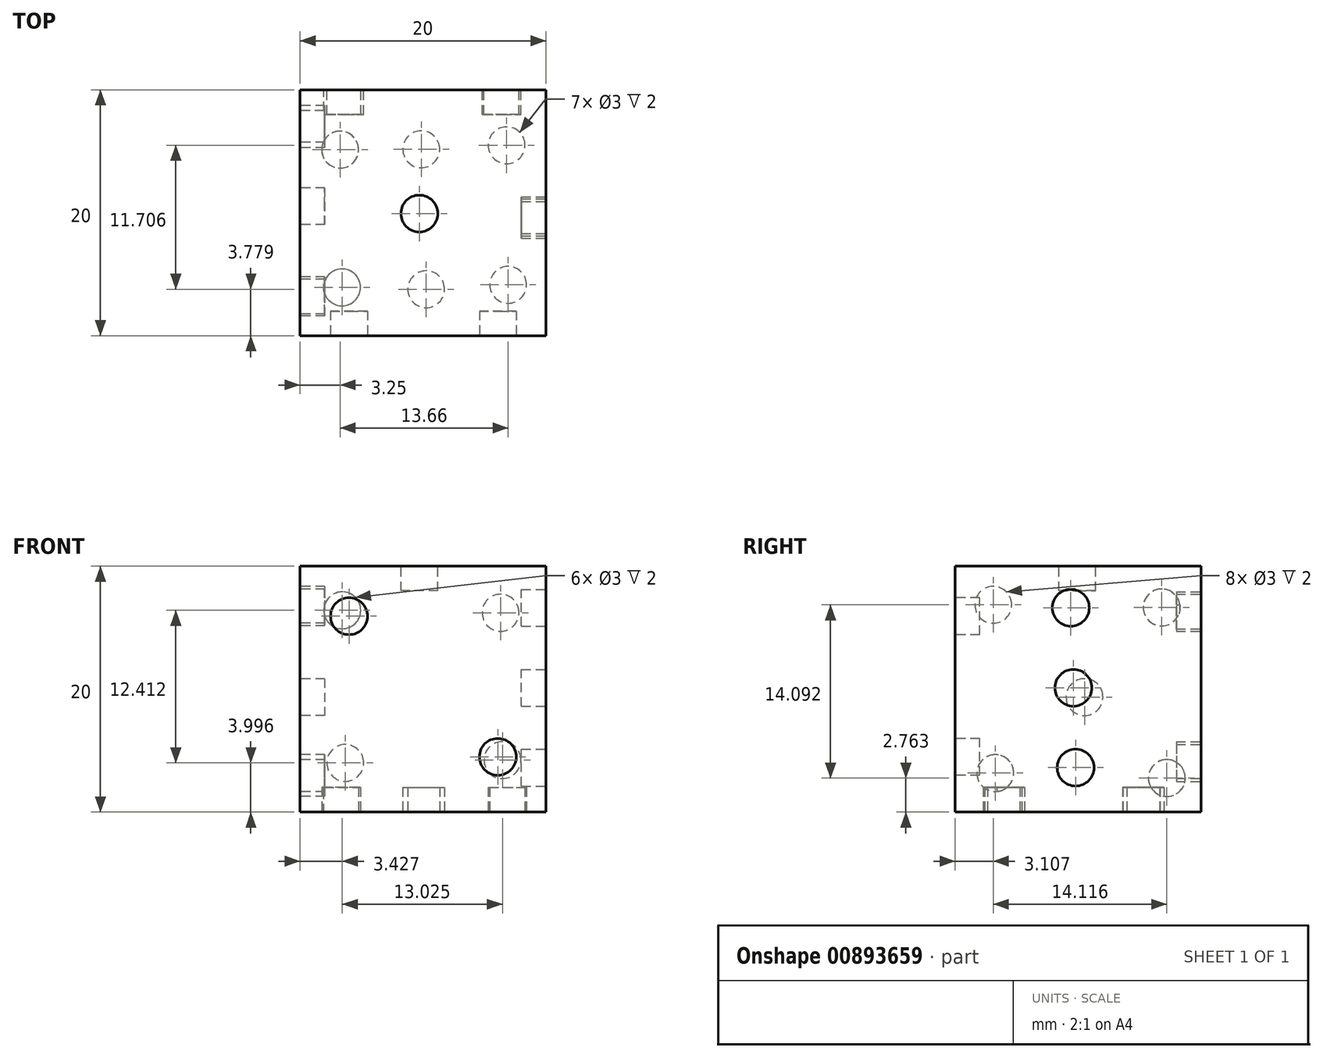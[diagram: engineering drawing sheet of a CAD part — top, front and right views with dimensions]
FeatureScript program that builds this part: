
annotation { "Feature Type Name" : "Feature", "Feature Type Description" : "" }
export const myFeature = defineFeature(function(context is Context, id is Id, definition is map)
    precondition{}
    {
        {
            var Q0;
            Q0=qCreatedBy(makeId("Top.planeOp"),FACE);
            var sketch = newSketch(context, id + "F0", { "sketchPlane" : qUnion([Q0])});
            skLineSegment(sketch, "E0.bottom", {"start": v(-32.53, -1.25) * mm, "end": v(-12.53, -1.25) * mm});
            skLineSegment(sketch, "E0.top", {"start": v(-32.53, -21.25) * mm, "end": v(-12.53, -21.25) * mm});
            skLineSegment(sketch, "E0.left", {"start": v(-32.53, -1.25) * mm, "end": v(-32.53, -21.25) * mm});
            skLineSegment(sketch, "E0.right", {"start": v(-12.53, -1.25) * mm, "end": v(-12.53, -21.25) * mm});
            skSolve(sketch);
        }
        {
            var Q0;
            Q0=makeQuery(id+"F0.imprint","IMPRINT",FACE,{"disambiguationData":[TD([[makeQuery(id+"F0.imprint","IMPRINT",EDGE,{"derivedFrom":sQuery(id+"F0.wireOp",EDGE,"E0.bottom")}),-1.0]])]});
            extrude(context, id + "F1", {"entities" : qUnion([Q0]), "depth" : 20 * mm, "offsetDistance" : 25 * mm});
        }
        {
            var Q0;
            Q0=makeQuery(id+"F1.opExtrude","CAP_FACE",FACE,{"disambiguationData":[OSD([sQuery(id+"F0.wireOp",EDGE,"E0.bottom"),sQuery(id+"F0.wireOp",EDGE,"E0.top"),sQuery(id+"F0.wireOp",EDGE,"E0.left"),sQuery(id+"F0.wireOp",EDGE,"E0.right")])],"isStart":false});
            var sketch = newSketch(context, id + "F2", { "sketchPlane" : qUnion([Q0])});
            skCircle(sketch, "E1", {"center": v(-22.83, -11.32) * mm, "radius": 1.5 * mm});
            skSolve(sketch);
        }
        {
            var Q0;
            Q0 = qSketchRegion(id + "F2", true);
            extrude(context, id + "F3", {"entities" : qUnion([Q0]), "operationType" : NewBodyOperationType.REMOVE, "oppositeDirection" : true, "depth" : 2 * mm, "offsetDistance" : 25 * mm});
        }
        {
            var Q0;
            Q0=makeQuery(id+"F1.opExtrude","SWEPT_FACE",FACE,{"disambiguationData":[OSD([sQuery(id+"F0.wireOp",EDGE,"E0.top")])]});
            var sketch = newSketch(context, id + "F4", { "sketchPlane" : qUnion([Q0])});
            skCircle(sketch, "E2", {"center": v(-28.56, 15.93) * mm, "radius": 1.5 * mm});
            skCircle(sketch, "E3", {"center": v(-16.45, 4.48) * mm, "radius": 1.5 * mm});
            skSolve(sketch);
        }
        {
            var Q0;
            Q0 = qSketchRegion(id + "F4", true);
            extrude(context, id + "F5", {"entities" : qUnion([Q0]), "operationType" : NewBodyOperationType.REMOVE, "oppositeDirection" : true, "depth" : 2 * mm, "offsetDistance" : 25 * mm});
        }
        {
            var Q0;
            Q0=makeQuery(id+"F1.opExtrude","SWEPT_FACE",FACE,{"disambiguationData":[OSD([sQuery(id+"F0.wireOp",EDGE,"E0.right")])]});
            var sketch = newSketch(context, id + "F6", { "sketchPlane" : qUnion([Q0])});
            skCircle(sketch, "E4", {"center": v(-11.84, 16.62) * mm, "radius": 1.5 * mm});
            skCircle(sketch, "E5", {"center": v(-11.45, 3.61) * mm, "radius": 1.5 * mm});
            skCircle(sketch, "E6", {"center": v(-11.63, 10.1) * mm, "radius": 1.5 * mm});
            skSolve(sketch);
        }
        {
            var Q0;
            Q0 = qSketchRegion(id + "F6", true);
            extrude(context, id + "F7", {"entities" : qUnion([Q0]), "operationType" : NewBodyOperationType.REMOVE, "oppositeDirection" : true, "depth" : 2 * mm, "offsetDistance" : 25 * mm});
        }
        {
            var Q0;
            Q0=makeQuery(id+"F1.opExtrude","SWEPT_FACE",FACE,{"disambiguationData":[OSD([sQuery(id+"F0.wireOp",EDGE,"E0.bottom")])]});
            var sketch = newSketch(context, id + "F8", { "sketchPlane" : qUnion([Q0])});
            skCircle(sketch, "E7", {"center": v(16.23, 16.21) * mm, "radius": 1.5 * mm});
            skCircle(sketch, "E8", {"center": v(29.1, 16.4) * mm, "radius": 1.5 * mm});
            skCircle(sketch, "E9", {"center": v(28.86, 4) * mm, "radius": 1.5 * mm});
            skCircle(sketch, "E10", {"center": v(16.08, 4.23) * mm, "radius": 1.5 * mm});
            skSolve(sketch);
        }
        {
            var Q0;
            Q0 = qSketchRegion(id + "F8", true);
            extrude(context, id + "F9", {"entities" : qUnion([Q0]), "operationType" : NewBodyOperationType.REMOVE, "oppositeDirection" : true, "depth" : 2 * mm, "offsetDistance" : 25 * mm});
        }
        {
            var Q0;
            Q0=makeQuery(id+"F1.opExtrude","SWEPT_FACE",FACE,{"disambiguationData":[OSD([sQuery(id+"F0.wireOp",EDGE,"E0.left")])]});
            var sketch = newSketch(context, id + "F10", { "sketchPlane" : qUnion([Q0])});
            skCircle(sketch, "E11", {"center": v(18.14, 16.86) * mm, "radius": 1.5 * mm});
            skCircle(sketch, "E12", {"center": v(17.98, 3.17) * mm, "radius": 1.5 * mm});
            skCircle(sketch, "E13", {"center": v(4.45, 16.64) * mm, "radius": 1.5 * mm});
            skCircle(sketch, "E14", {"center": v(10.72, 9.35) * mm, "radius": 1.5 * mm});
            skCircle(sketch, "E15", {"center": v(4.03, 2.76) * mm, "radius": 1.5 * mm});
            skSolve(sketch);
        }
        {
            var Q0;
            Q0 = qSketchRegion(id + "F10", true);
            extrude(context, id + "F11", {"entities" : qUnion([Q0]), "operationType" : NewBodyOperationType.REMOVE, "oppositeDirection" : true, "depth" : 2 * mm, "offsetDistance" : 25 * mm});
        }
        {
            var Q0;
            Q0=makeQuery(id+"F1.opExtrude","CAP_FACE",FACE,{"disambiguationData":[OSD([sQuery(id+"F0.wireOp",EDGE,"E0.bottom"),sQuery(id+"F0.wireOp",EDGE,"E0.top"),sQuery(id+"F0.wireOp",EDGE,"E0.left"),sQuery(id+"F0.wireOp",EDGE,"E0.right")])],"isStart":true});
            var sketch = newSketch(context, id + "F12", { "sketchPlane" : qUnion([Q0])});
            skCircle(sketch, "E16", {"center": v(-15.62, 17.11) * mm, "radius": 1.5 * mm});
            skCircle(sketch, "E17", {"center": v(-22.29, 17.47) * mm, "radius": 1.5 * mm});
            skCircle(sketch, "E18", {"center": v(-29.12, 17.32) * mm, "radius": 1.5 * mm});
            skCircle(sketch, "E19", {"center": v(-29.28, 6.11) * mm, "radius": 1.5 * mm});
            skCircle(sketch, "E20", {"center": v(-22.68, 6.09) * mm, "radius": 1.5 * mm});
            skCircle(sketch, "E21", {"center": v(-15.74, 5.76) * mm, "radius": 1.5 * mm});
            skSolve(sketch);
        }
        {
            var Q0;
            Q0 = qSketchRegion(id + "F12", true);
            extrude(context, id + "F13", {"entities" : qUnion([Q0]), "operationType" : NewBodyOperationType.REMOVE, "oppositeDirection" : true, "depth" : 2 * mm, "offsetDistance" : 25 * mm});
        }
    });
